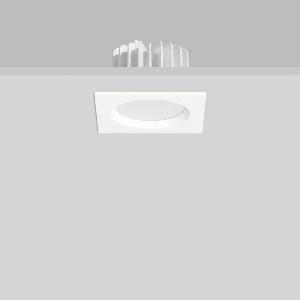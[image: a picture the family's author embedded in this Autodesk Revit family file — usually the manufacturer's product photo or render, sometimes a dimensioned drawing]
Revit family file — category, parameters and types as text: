
# Revit family: ledona_eco_square_901435_002_35c5
name_source: partatom
category: Lighting Fixtures
units: mm (PartAtom-declared; Revit-internal decimal feet)

## family parameters
Cut with Voids When Loaded = No
Host = Face
Light Source = No
Part Type = Normal
Room Calculation Point = No
Round Connector Dimension = Use Diameter
Shared = No

## types (1)
- LEDONA ECO square (1 x LED Modul 830, 660 lm, 3000)
    Apparent Load = 10 VA
    CIE Flux Codes = 49 81 97 100 100
    Color Rendering = 80
    Color Temperature = 3000
    Default Elevation = 1800 mm
    Height = 0 mm  [stored 0 ft]
    Lamp = 1 x LED Modul 830
    Lamp Light Flux = 660 lm
    Lamp count = 1
    Length = 130 mm
    Lifetime = 50000 h
    Luminous efficacy = 66 lm/W
    Manufacturer = RZB
    ModVariant = No
    Model = 901435.002
    Mounting Place = Ceiling
    Mounting Type = Recessed
    Number of Poles = 1
    OnlyDefault = Yes
    Power Factor = 1
    Product Name = LEDONA ECO square
    Product group = Recessed downlights
    ProductGroupID = 402
    Protection Class = Protection class I
    Protection Degree = IP 65
    RLX_Detail_Level = 1
    RLX_Emergency_Light_Flux = 0 lm
    RLX_Emergency_Type = 0
    RLX_Emergency_Type_DB = No
    RlxData = <blob elided: 28977 chars, md5=5bfc5a5e>
    Socket = socket
    Standby Power = 0 W
    System Light Flux = 660 lm
    System Power = 10 W
    Type Comments = Product without accessories
    Type Image = 901436.002.jpg
    URL = http://relux.com
    VarID = ---
    Voltage = 230 V
    Voltage Range = 220-240 V
    Weight = 0.00 kg
    Width = 130 mm

note: [stored X ft] marks values corroborated as IEEE doubles in the binary element streams (Revit-internal decimal feet)

## geometry (parser evidence)
native form markers: Blend x4, Sweep x10
no freeform markers — native parametric forms only
